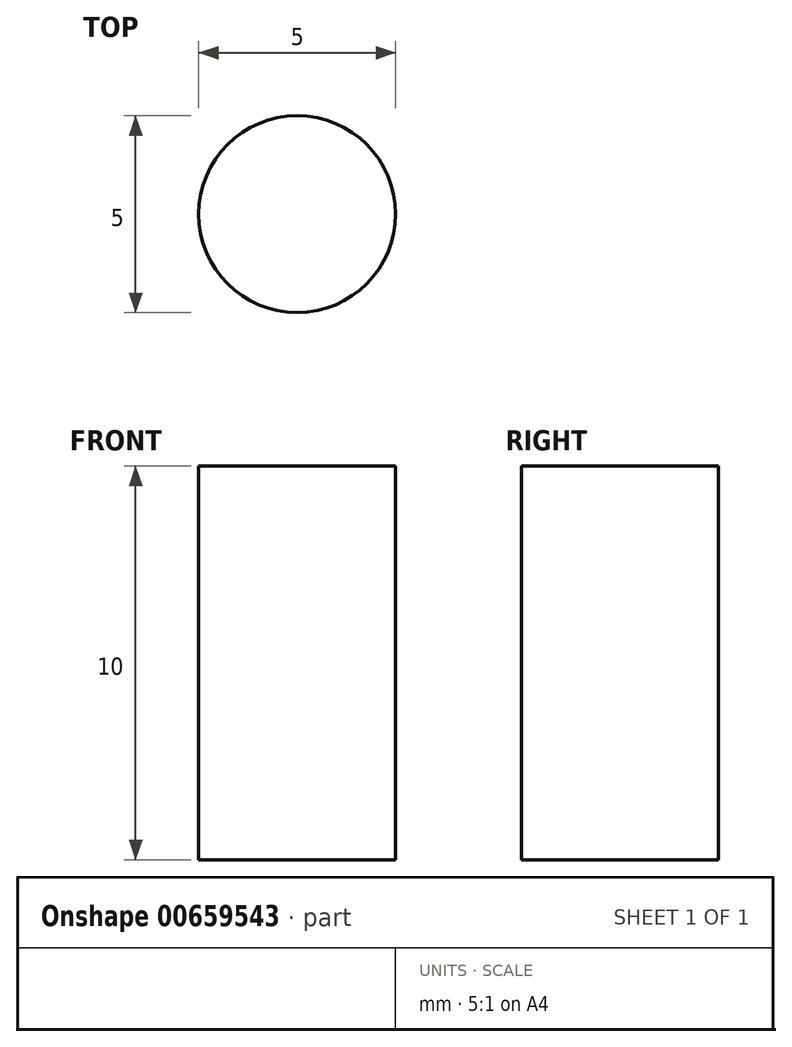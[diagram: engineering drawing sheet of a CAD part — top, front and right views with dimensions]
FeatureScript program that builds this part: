
annotation { "Feature Type Name" : "Feature", "Feature Type Description" : "" }
export const myFeature = defineFeature(function(context is Context, id is Id, definition is map)
    precondition{}
    {
        {
            var Q0;
            Q0=qCreatedBy(makeId("Top.planeOp"),FACE);
            var sketch = newSketch(context, id + "F0", { "sketchPlane" : qUnion([Q0])});
            skCircle(sketch, "E0", {"center": v(0, 0) * mm, "radius": 2.5 * mm});
            skSolve(sketch);
        }
        {
            var Q0;
            Q0=makeQuery(id+"F0.imprint","IMPRINT",FACE,{"disambiguationData":[TD([[makeQuery(id+"F0.imprint","IMPRINT",EDGE,{"derivedFrom":sQuery(id+"F0.wireOp",EDGE,"E0")}),1.0]])]});
            extrude(context, id + "F1", {"entities" : qUnion([Q0]), "depth" : 10 * mm, "offsetDistance" : 25 * mm});
        }
    });
